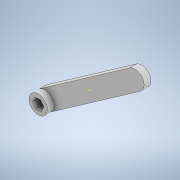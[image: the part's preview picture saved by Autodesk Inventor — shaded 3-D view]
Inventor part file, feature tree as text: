
AUTODESK INVENTOR PART (.ipt)
format: ipt  version: 2020.2 (Build 242310000, 310)  size: 123,904 bytes
history: native  units: in
note: dims shown in document units (in); Inventor stores cm internally (conversion verified against a paired STEP export)
features: sketch x4, extrude x3, fillet x1
ambient origin geometry x8: Origin, YZ Plane, XZ Plane, XY Plane, X Axis, Y Axis, Z Axis, Center Point
bodies: Solid1 (feature_tree)
feature tree (8):
  extrude  "Extrusion1"  Depth=1.0in
  sketch  "Sketch2"  dims[d3=0.375in d4=0.0in d5=0.5in]
  fillet  "Fillet1"  Radius=1.0in
  sketch  "Sketch3"  dims[d8=0.375in d9=0.0in d10=1.0in d11=0.0in]
  extrude  "Extrusion2"  Depth=0.5in
  extrude  "Extrusion3"  Depth=1.0in TaperAngle=0.0deg
  sketch  "Sketch1"  dims[d0=7.0in d1=0.2405in d2=1.0in]
  sketch  "Sketch4"
